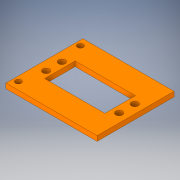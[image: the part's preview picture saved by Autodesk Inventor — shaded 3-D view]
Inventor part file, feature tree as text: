
AUTODESK INVENTOR PART (.ipt)
format: ipt  version: 2019 (Build 230136000, 136)  size: 141,312 bytes
history: native  units: mm
features: extrude x1, sketch x1
ambient origin geometry x8: Origin, YZ Plane, XZ Plane, XY Plane, X Axis, Y Axis, Z Axis, Center Point
bodies: Solid1 (feature_tree)
feature tree (2):
  extrude  "Extrusion1"  Depth=19.8mm
  sketch  "Sketch1"  dims[d0=39.0mm d1=19.8mm d2=10.0mm d3=10.0mm d4=15.0mm d5=15.0mm d6=4.38mm d7=4.38mm d8=5.085mm d9=5.085mm d10=3.81mm d11=3.81mm d12=47.26mm d13=47.26mm d14=4.38mm d15=4.38mm d16=5.085mm d17=5.085mm d18=3.81mm d19=3.81mm d20=15.0mm d21=15.0mm d22=3.0mm d23=3.0mm d24=3.18mm d25=0.0mm]
